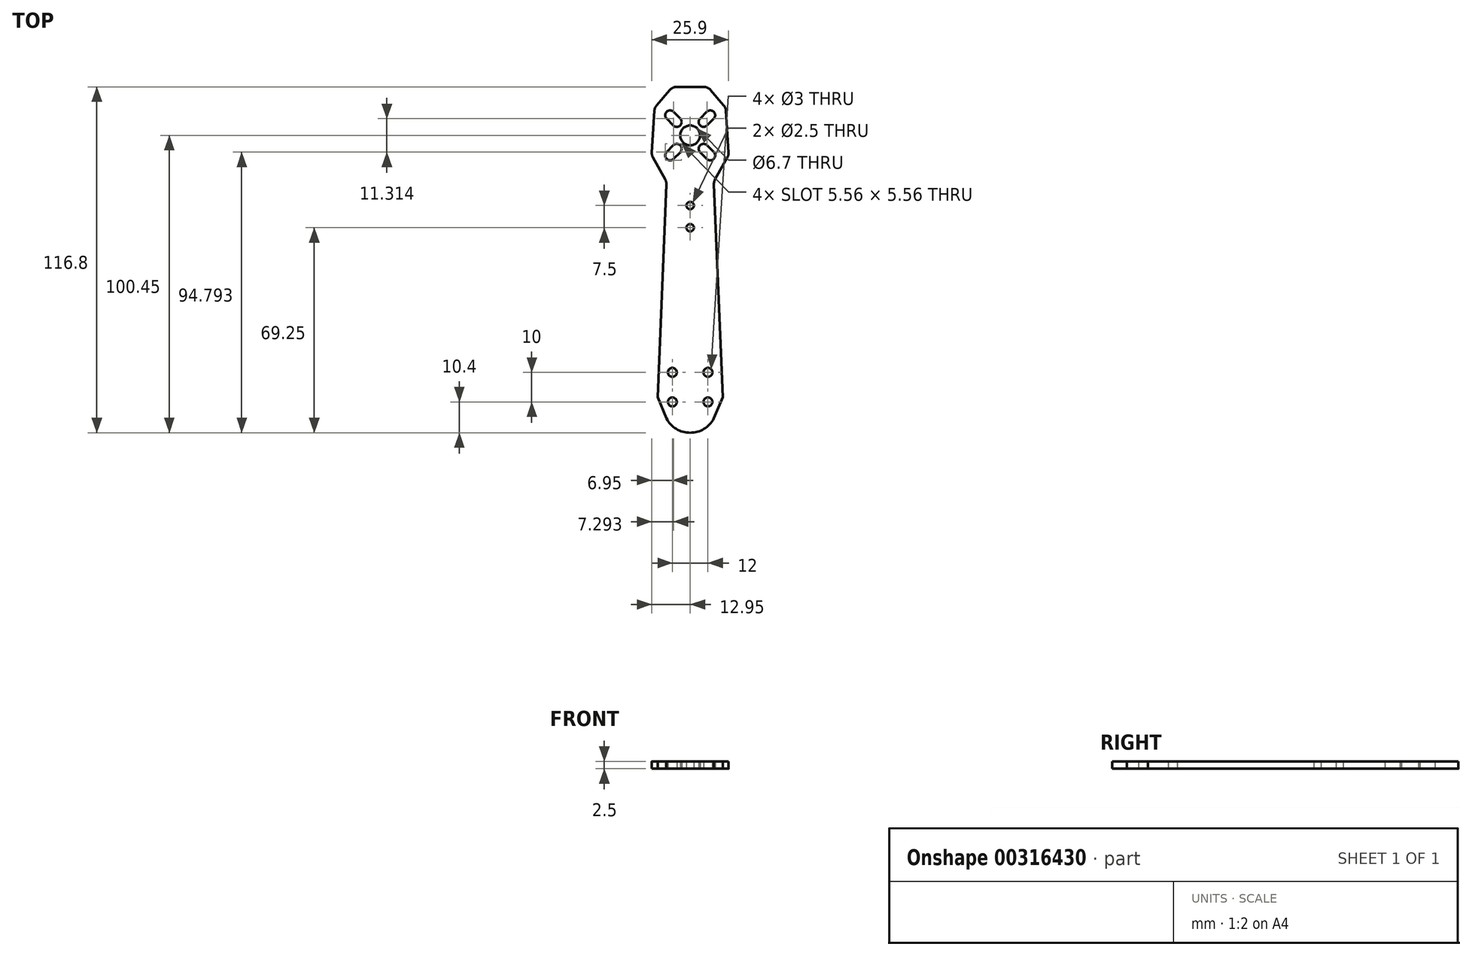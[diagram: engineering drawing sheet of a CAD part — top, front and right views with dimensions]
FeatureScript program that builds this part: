
annotation { "Feature Type Name" : "Feature", "Feature Type Description" : "" }
export const myFeature = defineFeature(function(context is Context, id is Id, definition is map)
    precondition{}
    {
        {
            var Q0;
            Q0=qCreatedBy(makeId("Top.planeOp"),FACE);
            var sketch = newSketch(context, id + "F0", { "sketchPlane" : qUnion([Q0])});
            skLineSegment(sketch, "E0", {"start": v(-11, -56) * mm, "end": v(-8.03, 15.96) * mm});
            skLineSegment(sketch, "E1", {"start": v(-8.4, 17.54) * mm, "end": v(-12.57, 25.03) * mm});
            skLineSegment(sketch, "E2", {"start": v(-12.95, 26.68) * mm, "end": v(-12.06, 40.8) * mm});
            skLineSegment(sketch, "E3", {"start": v(-11.35, 42.56) * mm, "end": v(-6.9, 47.75) * mm});
            skLineSegment(sketch, "E4", {"start": v(-4.62, 48.8) * mm, "end": v(4.62, 48.8) * mm});
            skLineSegment(sketch, "E5", {"start": v(6.9, 47.75) * mm, "end": v(11.35, 42.56) * mm});
            skLineSegment(sketch, "E6", {"start": v(12.06, 40.8) * mm, "end": v(12.95, 26.68) * mm});
            skLineSegment(sketch, "E7", {"start": v(12.57, 25.03) * mm, "end": v(8.4, 17.54) * mm});
            skLineSegment(sketch, "E8", {"start": v(8.03, 15.96) * mm, "end": v(11, -56) * mm});
            skLineSegment(sketch, "E9", {"start": v(11, -56) * mm, "end": v(8, -63.13) * mm});
            skLineSegment(sketch, "E10", {"start": v(-8, -63.13) * mm, "end": v(-11, -56) * mm});
            skPoint(sketch, "E11.visualSharp", {"position": v(0, -68) * mm});
            skArc(sketch, "E12", {"start": v(-8, -63.13) * mm, "mid": v(0, -68) * mm, "end": v(8, -63.13) * mm});
            skCircle(sketch, "E13", {"center": v(6, -47.6) * mm, "radius": 1.5 * mm});
            skCircle(sketch, "E14", {"center": v(-6, -47.6) * mm, "radius": 1.5 * mm});
            skCircle(sketch, "E15", {"center": v(6, -57.6) * mm, "radius": 1.5 * mm});
            skCircle(sketch, "E16", {"center": v(-6, -57.6) * mm, "radius": 1.5 * mm});
            skLineSegment(sketch, "E17", {"start": v(0, -68) * mm, "end": v(9.63, -68) * mm, "construction": true});
            skCircle(sketch, "E18", {"center": v(0, 1.25) * mm, "radius": 1.25 * mm});
            skCircle(sketch, "E19", {"center": v(0, 8.75) * mm, "radius": 1.25 * mm});
            skCircle(sketch, "E20", {"center": v(0, 32.45) * mm, "radius": 3.35 * mm});
            skPoint(sketch, "E20.centerSnap0", {"position": v(0, 48.8) * mm});
            skLineSegment(sketch, "E21", {"start": v(0, 32.45) * mm, "end": v(4.53, 27.92) * mm, "construction": true});
            skLineSegment(sketch, "E22", {"start": v(0, 32.45) * mm, "end": v(4.53, 36.98) * mm, "construction": true});
            skLineSegment(sketch, "E23", {"start": v(4.53, 36.98) * mm, "end": v(6.79, 39.24) * mm});
            skArc(sketch, "E24.0.startCap", {"start": v(5.7, 35.8) * mm, "mid": v(3.36, 35.8) * mm, "end": v(3.36, 38.14) * mm});
            skArc(sketch, "E24.0.endCap", {"start": v(5.62, 40.4) * mm, "mid": v(7.95, 40.4) * mm, "end": v(7.95, 38.07) * mm});
            skLineSegment(sketch, "E24.0.left", {"start": v(3.36, 38.14) * mm, "end": v(5.62, 40.4) * mm});
            skLineSegment(sketch, "E24.0.right", {"start": v(5.7, 35.8) * mm, "end": v(7.95, 38.07) * mm});
            skLineSegment(sketch, "E25.MirrorCS", {"start": v(-4.53, 36.98) * mm, "end": v(-6.79, 39.24) * mm});
            skLineSegment(sketch, "E26.MirrorCS", {"start": v(-4.53, 27.92) * mm, "end": v(-6.79, 25.66) * mm});
            skLineSegment(sketch, "E27.MirrorCS", {"start": v(4.53, 27.92) * mm, "end": v(6.79, 25.66) * mm});
            skArc(sketch, "E28.0.startCap", {"start": v(-3.36, 38.14) * mm, "mid": v(-3.36, 35.8) * mm, "end": v(-5.7, 35.8) * mm});
            skArc(sketch, "E28.0.endCap", {"start": v(-7.95, 38.07) * mm, "mid": v(-7.95, 40.4) * mm, "end": v(-5.62, 40.4) * mm});
            skLineSegment(sketch, "E28.0.left", {"start": v(-5.7, 35.8) * mm, "end": v(-7.95, 38.07) * mm});
            skLineSegment(sketch, "E28.0.right", {"start": v(-3.36, 38.14) * mm, "end": v(-5.62, 40.4) * mm});
            skArc(sketch, "E29.0.startCap", {"start": v(3.36, 26.76) * mm, "mid": v(3.36, 29.1) * mm, "end": v(5.7, 29.1) * mm});
            skArc(sketch, "E29.0.endCap", {"start": v(7.95, 26.83) * mm, "mid": v(7.95, 24.5) * mm, "end": v(5.62, 24.5) * mm});
            skLineSegment(sketch, "E29.0.left", {"start": v(5.7, 29.1) * mm, "end": v(7.95, 26.83) * mm});
            skLineSegment(sketch, "E29.0.right", {"start": v(3.36, 26.76) * mm, "end": v(5.62, 24.5) * mm});
            skArc(sketch, "E30.0.startCap", {"start": v(-5.7, 29.1) * mm, "mid": v(-3.36, 29.1) * mm, "end": v(-3.36, 26.76) * mm});
            skArc(sketch, "E30.0.endCap", {"start": v(-5.62, 24.5) * mm, "mid": v(-7.95, 24.5) * mm, "end": v(-7.95, 26.83) * mm});
            skLineSegment(sketch, "E30.0.left", {"start": v(-3.36, 26.76) * mm, "end": v(-5.62, 24.5) * mm});
            skLineSegment(sketch, "E30.0.right", {"start": v(-5.7, 29.1) * mm, "end": v(-7.95, 26.83) * mm});
            skPoint(sketch, "E31.visualSharp", {"position": v(-12, 41.8) * mm});
            skArc(sketch, "E31.filletArc", {"start": v(-11.35, 42.56) * mm, "mid": v(-11.85, 41.74) * mm, "end": v(-12.06, 40.8) * mm});
            skPoint(sketch, "E32.visualSharp", {"position": v(-6, 48.8) * mm});
            skArc(sketch, "E32.filletArc", {"start": v(-4.62, 48.8) * mm, "mid": v(-5.87, 48.53) * mm, "end": v(-6.9, 47.75) * mm});
            skPoint(sketch, "E33.visualSharp", {"position": v(6, 48.8) * mm});
            skArc(sketch, "E33.filletArc", {"start": v(6.9, 47.75) * mm, "mid": v(5.87, 48.53) * mm, "end": v(4.62, 48.8) * mm});
            skPoint(sketch, "E34.visualSharp", {"position": v(12, 41.8) * mm});
            skArc(sketch, "E34.filletArc", {"start": v(12.06, 40.8) * mm, "mid": v(11.85, 41.74) * mm, "end": v(11.35, 42.56) * mm});
            skPoint(sketch, "E35.visualSharp", {"position": v(13, 25.8) * mm});
            skArc(sketch, "E35.filletArc", {"start": v(12.57, 25.03) * mm, "mid": v(12.88, 25.83) * mm, "end": v(12.95, 26.68) * mm});
            skPoint(sketch, "E36.visualSharp", {"position": v(8, 16.8) * mm});
            skArc(sketch, "E36.filletArc", {"start": v(8.4, 17.54) * mm, "mid": v(8.11, 16.77) * mm, "end": v(8.03, 15.96) * mm});
            skPoint(sketch, "E37.visualSharp", {"position": v(-8, 16.8) * mm});
            skArc(sketch, "E37.filletArc", {"start": v(-8.03, 15.96) * mm, "mid": v(-8.11, 16.77) * mm, "end": v(-8.4, 17.54) * mm});
            skPoint(sketch, "E38.visualSharp", {"position": v(-13, 25.8) * mm});
            skArc(sketch, "E38.filletArc", {"start": v(-12.95, 26.68) * mm, "mid": v(-12.88, 25.83) * mm, "end": v(-12.57, 25.03) * mm});
            skSolve(sketch);
        }
        {
            var Q0;
            Q0 = qSketchRegion(id + "F0", true);
            extrude(context, id + "F1", {"entities" : qUnion([Q0]), "depth" : 2.5 * mm});
        }
    });
